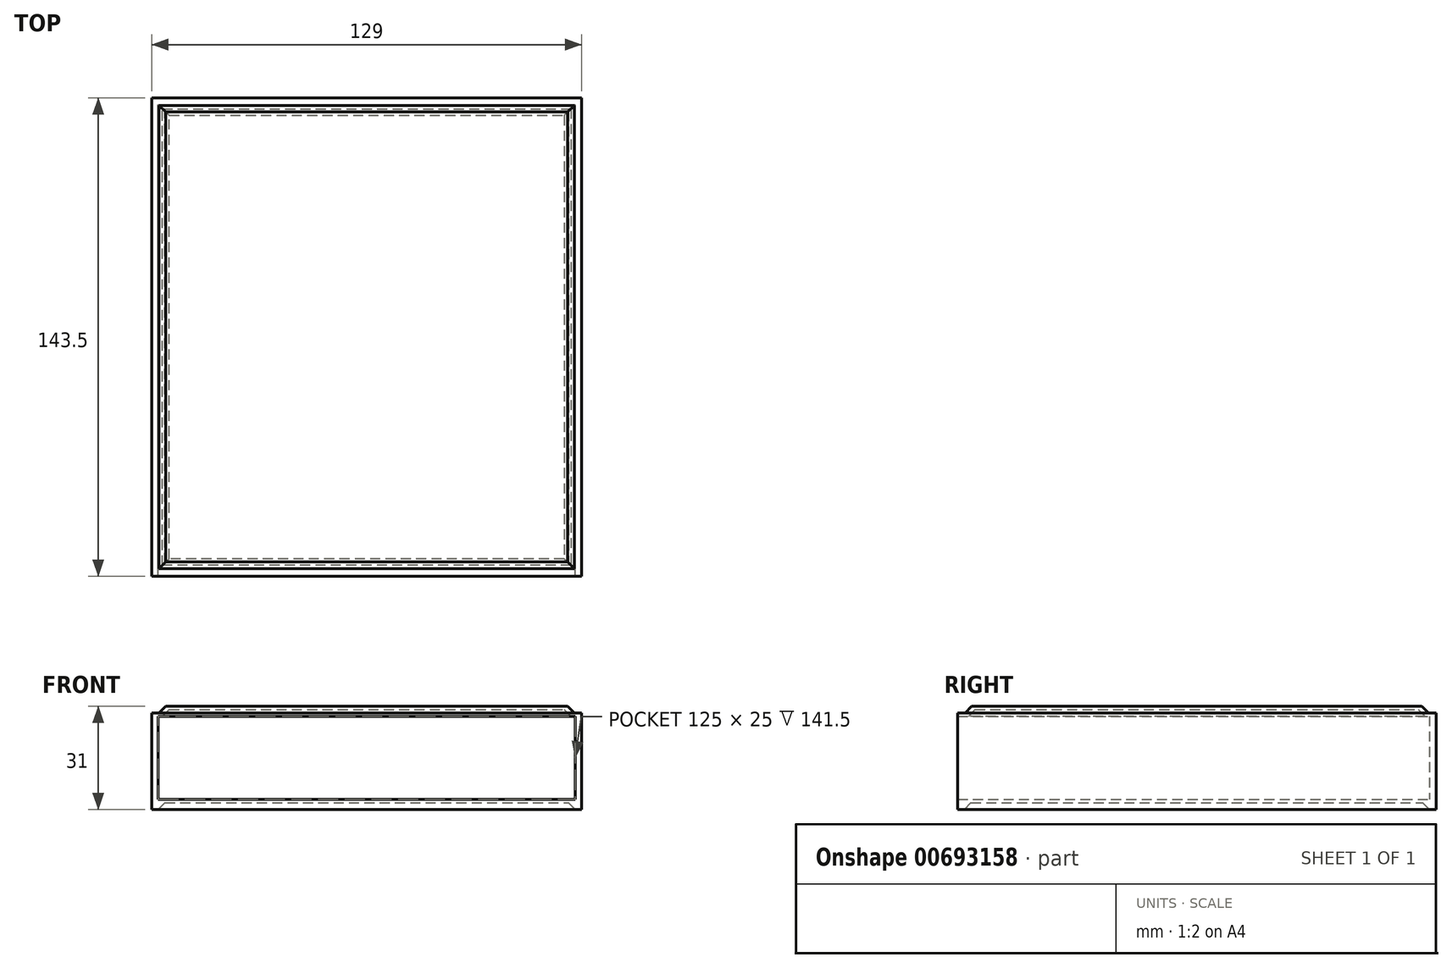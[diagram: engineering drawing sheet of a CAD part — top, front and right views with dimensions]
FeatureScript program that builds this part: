
annotation { "Feature Type Name" : "Feature", "Feature Type Description" : "" }
export const myFeature = defineFeature(function(context is Context, id is Id, definition is map)
    precondition{}
    {
        {
            var Q0;
            Q0=qCreatedBy(makeId("Top.planeOp"),FACE);
            var sketch = newSketch(context, id + "F0", { "sketchPlane" : qUnion([Q0])});
            skLineSegment(sketch, "E0.bottom", {"start": v(64.5, -71.75) * mm, "end": v(-64.5, -71.75) * mm});
            skLineSegment(sketch, "E0.top", {"start": v(64.5, 71.75) * mm, "end": v(-64.5, 71.75) * mm});
            skLineSegment(sketch, "E0.left", {"start": v(64.5, -71.75) * mm, "end": v(64.5, 71.75) * mm});
            skLineSegment(sketch, "E0.right", {"start": v(-64.5, -71.75) * mm, "end": v(-64.5, 71.75) * mm});
            skPoint(sketch, "E0.middle", {"position": v(0, 0) * mm});
            skLineSegment(sketch, "E1.bottom", {"start": v(62.5, -69.75) * mm, "end": v(-62.5, -69.75) * mm});
            skLineSegment(sketch, "E1.top", {"start": v(62.5, 69.75) * mm, "end": v(-62.5, 69.75) * mm});
            skLineSegment(sketch, "E1.left", {"start": v(62.5, -69.75) * mm, "end": v(62.5, 69.75) * mm});
            skLineSegment(sketch, "E1.right", {"start": v(-62.5, -69.75) * mm, "end": v(-62.5, 69.75) * mm});
            skSolve(sketch);
        }
        {
            var Q0;
            Q0=makeQuery(id+"F0.imprint","IMPRINT",FACE,{"disambiguationData":[TD([[makeQuery(id+"F0.imprint","IMPRINT",EDGE,{"derivedFrom":sQuery(id+"F0.wireOp",EDGE,"E0.bottom")}),-1.0]])]});
            var Q1;
            Q1=makeQuery(id+"F0.imprint","IMPRINT",FACE,{"disambiguationData":[TD([[makeQuery(id+"F0.imprint","IMPRINT",EDGE,{"derivedFrom":sQuery(id+"F0.wireOp",EDGE,"E1.bottom")}),-1.0]])]});
            extrude(context, id + "F1", {"entities" : qUnion([Q0, Q1]), "depth" : 3 * mm, "offsetDistance" : 25 * mm});
        }
        {
            var Q0;
            Q0=makeQuery(id+"F0.imprint","IMPRINT",FACE,{"disambiguationData":[TD([[makeQuery(id+"F0.imprint","IMPRINT",EDGE,{"derivedFrom":sQuery(id+"F0.wireOp",EDGE,"E1.bottom")}),-1.0]])]});
            extrude(context, id + "F2", {"entities" : qUnion([Q0]), "operationType" : NewBodyOperationType.REMOVE, "depth" : 2 * mm, "offsetDistance" : 25 * mm});
        }
        {
            var Q0;
            Q0=makeQuery(id+"F2.boolean.opBoolean","COPY",FACE,{"derivedFrom":makeQuery(id+"F2.opExtrude","CAP_FACE",FACE,{"disambiguationData":[OSD([sQuery(id+"F0.wireOp",EDGE,"E1.bottom"),sQuery(id+"F0.wireOp",EDGE,"E1.top"),sQuery(id+"F0.wireOp",EDGE,"E1.left"),sQuery(id+"F0.wireOp",EDGE,"E1.right")])],"isStart":false})});
            chamfer(context, id + "F3", {"entities" : qUnion([Q0]), "width" : 2 * mm, "tangentPropagation" : true});
        }
        {
            var Q0;
            Q0=makeQuery(id+"F1.opExtrude","CAP_FACE",FACE,{"disambiguationData":[OSD([sQuery(id+"F0.wireOp",EDGE,"E0.bottom"),sQuery(id+"F0.wireOp",EDGE,"E0.top"),sQuery(id+"F0.wireOp",EDGE,"E0.left"),sQuery(id+"F0.wireOp",EDGE,"E0.right")])],"isStart":false});
            var sketch = newSketch(context, id + "F4", { "sketchPlane" : qUnion([Q0])});
            skLineSegment(sketch, "E2.bottom", {"start": v(-64.5, -71.75) * mm, "end": v(64.5, -71.75) * mm});
            skLineSegment(sketch, "E2.top", {"start": v(-64.5, 71.75) * mm, "end": v(64.5, 71.75) * mm});
            skLineSegment(sketch, "E2.left", {"start": v(-64.5, -71.75) * mm, "end": v(-64.5, 71.75) * mm});
            skLineSegment(sketch, "E2.right", {"start": v(64.5, -71.75) * mm, "end": v(64.5, 71.75) * mm});
            skLineSegment(sketch, "E3.bottom", {"start": v(-62.5, -71.75) * mm, "end": v(62.5, -71.75) * mm});
            skLineSegment(sketch, "E3.top", {"start": v(-62.5, 69.75) * mm, "end": v(62.5, 69.75) * mm});
            skLineSegment(sketch, "E3.left", {"start": v(-62.5, -71.75) * mm, "end": v(-62.5, 69.75) * mm});
            skLineSegment(sketch, "E3.right", {"start": v(62.5, -71.75) * mm, "end": v(62.5, 69.75) * mm});
            skSolve(sketch);
        }
        {
            var Q0;
            Q0=makeQuery(id+"F4.imprint","IMPRINT",FACE,{"disambiguationData":[TD([[makeQuery(id+"F4.imprint","IMPRINT",EDGE,{"derivedFrom":sQuery(id+"F4.wireOp",EDGE,"E2.top")}),1.0]])]});
            extrude(context, id + "F5", {"entities" : qUnion([Q0]), "operationType" : NewBodyOperationType.ADD, "depth" : 25 * mm, "offsetDistance" : 25 * mm});
        }
        {
            var Q0;
            Q0=makeQuery(id+"F5.opExtrude","CAP_FACE",FACE,{"disambiguationData":[OSD([sQuery(id+"F4.wireOp",EDGE,"E2.bottom"),sQuery(id+"F4.wireOp",EDGE,"E2.top"),sQuery(id+"F4.wireOp",EDGE,"E2.left"),sQuery(id+"F4.wireOp",EDGE,"E2.right"),sQuery(id+"F4.wireOp",EDGE,"E3.top"),sQuery(id+"F4.wireOp",EDGE,"E3.left"),sQuery(id+"F4.wireOp",EDGE,"E3.right")])],"isStart":false});
            var sketch = newSketch(context, id + "F6", { "sketchPlane" : qUnion([Q0])});
            skLineSegment(sketch, "E4.bottom", {"start": v(-64.5, -71.75) * mm, "end": v(64.5, -71.75) * mm});
            skLineSegment(sketch, "E4.top", {"start": v(-64.5, 71.75) * mm, "end": v(64.5, 71.75) * mm});
            skLineSegment(sketch, "E4.left", {"start": v(-64.5, -71.75) * mm, "end": v(-64.5, 71.75) * mm});
            skLineSegment(sketch, "E4.right", {"start": v(64.5, -71.75) * mm, "end": v(64.5, 71.75) * mm});
            skLineSegment(sketch, "E5.bottom", {"start": v(-62.25, 69.5) * mm, "end": v(62.25, 69.5) * mm});
            skLineSegment(sketch, "E5.top", {"start": v(-62.25, -69.5) * mm, "end": v(62.25, -69.5) * mm});
            skLineSegment(sketch, "E5.left", {"start": v(-62.25, 69.5) * mm, "end": v(-62.25, -69.5) * mm});
            skLineSegment(sketch, "E5.right", {"start": v(62.25, 69.5) * mm, "end": v(62.25, -69.5) * mm});
            skLineSegment(sketch, "E6.bottom", {"start": v(-61.25, 68.5) * mm, "end": v(61.25, 68.5) * mm});
            skLineSegment(sketch, "E6.top", {"start": v(-61.25, -68.5) * mm, "end": v(61.25, -68.5) * mm});
            skLineSegment(sketch, "E6.left", {"start": v(-61.25, 68.5) * mm, "end": v(-61.25, -68.5) * mm});
            skLineSegment(sketch, "E6.right", {"start": v(61.25, 68.5) * mm, "end": v(61.25, -68.5) * mm});
            skSolve(sketch);
        }
        {
            var Q0;
            Q0=makeQuery(id+"F6.imprint","IMPRINT",FACE,{"disambiguationData":[TD([[makeQuery(id+"F6.imprint","IMPRINT",EDGE,{"derivedFrom":sQuery(id+"F6.wireOp",EDGE,"E5.bottom")}),1.0]])]});
            var Q1;
            Q1=makeQuery(id+"F6.imprint","IMPRINT",FACE,{"disambiguationData":[TD([[makeQuery(id+"F6.imprint","IMPRINT",EDGE,{"derivedFrom":sQuery(id+"F6.wireOp",EDGE,"E4.top")}),1.0]])]});
            var Q2;
            Q2=makeQuery(id+"F6.imprint","IMPRINT",FACE,{"disambiguationData":[TD([[makeQuery(id+"F6.imprint","IMPRINT",EDGE,{"derivedFrom":sQuery(id+"F6.wireOp",EDGE,"E6.bottom")}),-1.0]])]});
            var Q3;
            Q3=makeQuery(id+"F6.imprint","IMPRINT",FACE,{"disambiguationData":[TD([[makeQuery(id+"F6.imprint","IMPRINT",EDGE,{"derivedFrom":sQuery(id+"F6.wireOp",EDGE,"E5.bottom")}),-1.0]])]});
            extrude(context, id + "F7", {"entities" : qUnion([Q0, Q1, Q2, Q3]), "operationType" : NewBodyOperationType.ADD, "depth" : 1 * mm, "offsetDistance" : 25 * mm});
        }
        {
            var Q0;
            Q0=makeQuery(id+"F6.imprint","IMPRINT",FACE,{"disambiguationData":[TD([[makeQuery(id+"F6.imprint","IMPRINT",EDGE,{"derivedFrom":sQuery(id+"F6.wireOp",EDGE,"E6.bottom")}),-1.0]])]});
            var Q1;
            Q1=makeQuery(id+"F6.imprint","IMPRINT",FACE,{"disambiguationData":[TD([[makeQuery(id+"F6.imprint","IMPRINT",EDGE,{"derivedFrom":sQuery(id+"F6.wireOp",EDGE,"E5.bottom")}),-1.0]])]});
            extrude(context, id + "F8", {"entities" : qUnion([Q0, Q1]), "operationType" : NewBodyOperationType.ADD, "depth" : 3 * mm, "offsetDistance" : 25 * mm});
        }
        {
            var Q0;
            Q0=makeQuery(id+"F8.opExtrude","CAP_EDGE",EDGE,{"disambiguationData":[OSD([sQuery(id+"F6.wireOp",EDGE,"d14ea8a3-13da-46dc-b887-d83dcd02b8a7.bottom")])],"isStart":false});
            var Q1;
            Q1=makeQuery(id+"F8.opExtrude","CAP_EDGE",EDGE,{"disambiguationData":[OSD([sQuery(id+"F4.wireOp",EDGE,"E3.left")])],"isStart":false});
            var Q2;
            Q2=makeQuery(id+"F8.opExtrude","CAP_EDGE",EDGE,{"disambiguationData":[OSD([sQuery(id+"F6.wireOp",EDGE,"d14ea8a3-13da-46dc-b887-d83dcd02b8a7.right")])],"isStart":false});
            var Q3;
            Q3=makeQuery(id+"F8.opExtrude","CAP_EDGE",EDGE,{"disambiguationData":[OSD([sQuery(id+"F6.wireOp",EDGE,"d14ea8a3-13da-46dc-b887-d83dcd02b8a7.top")])],"isStart":false});
            var Q4;
            Q4=makeQuery(id+"F8.opExtrude","CAP_FACE",FACE,{"disambiguationData":[OSD([sQuery(id+"F6.wireOp",EDGE,"E5.bottom"),sQuery(id+"F6.wireOp",EDGE,"E5.top"),sQuery(id+"F6.wireOp",EDGE,"E5.left"),sQuery(id+"F6.wireOp",EDGE,"E5.right")])],"isStart":false});
            chamfer(context, id + "F9", {"entities" : qUnion([Q0, Q1, Q2, Q3, Q4]), "width" : 2 * mm, "tangentPropagation" : true});
        }
        {
            var Q0;
            Q0=makeQuery(id+"F6.imprint","IMPRINT",FACE,{"disambiguationData":[TD([[makeQuery(id+"F6.imprint","IMPRINT",EDGE,{"derivedFrom":sQuery(id+"F6.wireOp",EDGE,"E6.bottom")}),-1.0]])]});
            extrude(context, id + "F10", {"entities" : qUnion([Q0]), "operationType" : NewBodyOperationType.REMOVE, "depth" : 2 * mm, "offsetDistance" : 25 * mm, "hasDraft" : true, "draftAngle" : 45 * degree, "draftPullDirection" : true});
        }
    });
